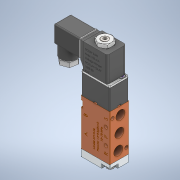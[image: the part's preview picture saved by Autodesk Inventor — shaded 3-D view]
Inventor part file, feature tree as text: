
AUTODESK INVENTOR PART (.ipt)
format: ipt  version: 2020 (Build 240168000, 168)  size: 15,170,048 bytes
history: native  units: in
note: dims shown in document units (in); Inventor stores cm internally (conversion verified against a paired STEP export)
features: other x76, pattern_circular x1, sketch x1
ambient origin geometry x8: Origin, YZ Plane, XZ Plane, XY Plane, X Axis, Y Axis, Z Axis, Center Point
bodies: Solid1 (feature_tree), Solid2 (feature_tree), Solid3 (feature_tree), Solid4 (feature_tree), Solid5 (feature_tree), Solid6 (feature_tree), Solid7 (feature_tree), Solid8 (feature_tree), Solid9 (feature_tree), Solid10 (feature_tree), Solid11 (feature_tree), Solid12 (feature_tree), Solid13 (feature_tree), Solid14 (feature_tree), Solid15 (feature_tree), Solid16 (feature_tree), Solid17 (feature_tree), Solid18 (feature_tree), Solid19 (feature_tree), Solid20 (feature_tree), Solid21 (feature_tree), Solid22 (feature_tree), Solid23 (feature_tree), Solid24 (feature_tree), Solid25 (feature_tree), Solid26 (feature_tree), Solid27 (feature_tree), Solid28 (feature_tree), Solid29 (feature_tree), Solid30 (feature_tree), Solid31 (feature_tree), Solid32 (feature_tree), Solid33 (feature_tree), Solid34 (feature_tree), Solid35 (feature_tree), Solid36 (feature_tree), Solid37 (feature_tree), Solid38 (feature_tree), Solid39 (feature_tree), Solid40 (feature_tree), Solid41 (feature_tree), Solid42 (feature_tree), Solid43 (feature_tree), Solid44 (feature_tree), Solid45 (feature_tree), Solid46 (feature_tree), Solid47 (feature_tree), Solid48 (feature_tree), Solid49 (feature_tree), Solid50 (feature_tree), Solid51 (feature_tree), Solid52 (feature_tree), Solid53 (feature_tree), Solid54 (feature_tree), Solid55 (feature_tree), Solid56 (feature_tree), Solid57 (feature_tree), Solid58 (feature_tree), Solid59 (feature_tree), Solid60 (feature_tree), Solid61 (feature_tree), Solid62 (feature_tree), Solid63 (feature_tree), Solid64 (feature_tree), Solid65 (feature_tree), Solid66 (feature_tree), Solid67 (feature_tree), Solid68 (feature_tree), Solid69 (feature_tree), Solid70 (feature_tree), Solid71 (feature_tree), Solid72 (feature_tree), Solid73 (feature_tree), Solid74 (feature_tree), Solid75 (feature_tree), Solid76 (feature_tree), Solid77 (feature_tree), Solid78 (feature_tree), Solid79 (feature_tree), Solid80 (feature_tree), Solid81 (feature_tree), Solid82 (feature_tree), Solid83 (feature_tree), Solid84 (feature_tree), Solid85 (feature_tree), Solid86 (feature_tree)
feature tree (78):
  other  "Repaired Geometry1"
  pattern_circular  "Circular Pattern1"  Count=2 Angle=360.0deg
  sketch  "3D Sketch14"
  other  "Pattern of Solid36:1"
  other  "Pattern of Solid37:2"
  other  "Pattern of Solid38:3"
  other  "Pattern of Solid39:4"
  other  "Pattern of Solid40:5"
  other  "Pattern of Solid41:6"
  other  "Pattern of Solid42:7"
  other  "Pattern of Solid43:8"
  other  "Pattern of Solid44:9"
  other  "Pattern of Solid45:10"
  other  "Pattern of Solid46:11"
  other  "Pattern of Solid47:12"
  other  "Pattern of Solid48:13"
  other  "Pattern of Solid49:14"
  other  "Pattern of Solid50:15"
  other  "Pattern of Solid51:16"
  other  "Pattern of Solid52:17"
  other  "Pattern of Solid53:18"
  other  "Pattern of Solid54:19"
  other  "Pattern of Solid55:20"
  other  "VALVE BODY, 4V110-06, 2 POSITION, 5 WAY SOLENOID VALVE_74:1"
  other  "ACTUATING SHAFT, 4V110-06, 2 POSITION, 5 WAY SOLENOID VALVE_75:1"
  other  "O-RING, ACTUATING SHAFT, 4V110-06, 2 POSITION, 5 WAY SOLENOID VALVE_76:1"
  other  "O-RING, ACTUATING SHAFT, 4V110-06, 2 POSITION, 5 WAY SOLENOID VALVE_77:1"
  other  "LARGE O-RING, ACTUATING SHAFT, 4V110-06, 2 POSITION, 5 WAY SOLENOID VALVE_78:1"
  other  "INTERNAL SPRING, VALVE BODY SUBASSY, 4V110-06, 2 POSITION, 5 WAY SOLENOID VALVE_79:1"
  other  "SEALING BASE, VALVE BODY SUBASSY, 4V110-06, 2 POSITION, 5 WAY SOLENOID VALVE_80:1"
  other  "O-RING, SEALING BASE, VALVE BODY SUBASSY, 4V110-06, 2 POSITION, 5 WAY SOLENOID VALVE_81:1"
  other  "LARGE O-RING, ACTUATING SHAFT, 4V110-06, 2 POSITION, 5 WAY SOLENOID VALVE_86:1"
  other  "O-RING, ACTUATING SHAFT, 4V110-06, 2 POSITION, 5 WAY SOLENOID VALVE_87:1"
  other  "O-RING, ACTUATING SHAFT, 4V110-06, 2 POSITION, 5 WAY SOLENOID VALVE_88:1"
  other  "AIR ENTRY MANIFOLD, AIR DELIVERY SUBASSY, 4V110-06, 2 POSITION, 5 WAY SOLENOID VALVE_62:1"
  other  "SEAL PLATE, AIR DELIVERY SUBASSY, 4V110-06, 2 POSITION, 5 WAY SOLENOID VALVE_63:1"
  other  "SEAL, AIR DELIVERY SUBASSY, 4V110-06, 2 POSITION, 5 WAY SOLENOID VALVE_64:1"
  other  "LEVER, MANUAL CONTROL SUBASSY, 4V110-06, 2 POSITION, 5 WAY SOLENOID VALVE_71:1"
  other  "O-RING, MANUAL CONTROL SUBASSY, 4V110-06, 2 POSITION, 5 WAY SOLENOID VALVE_72:1"
  other  "SPRING, MANUAL CONTROL SUBASSY, 4V110-06, 2 POSITION, 5 WAY SOLENOID VALVE_73:1"
  other  "AIR LOCK TAB, AIR DELIVERY SUBASSY, 4V110-06, 2 POSITION, 5 WAY SOLENOID VALVE_66:1"
  other  "O-RING, AIR DELIVERY SUBASSY, 4V110-06, 2 POSITION, 5 WAY SOLENOID VALVE_67:1"
  other  "COMPRESSING PLATE, 4V110-06, 2 POSITION, 5 WAY SOLENOID VALVE_68:1"
  other  "MANIFOLD SEALING PIN, AIR DELIVERY SUBASSY, 4V110-06, 2 POSITION, 5 WAY SOLENOID VALVE_69:1"
  other  "MANIFOLD SEALING PIN, AIR DELIVERY SUBASSY, 4V110-06, 2 POSITION, 5 WAY SOLENOID VALVE_70:1"
  other  "SOLENOID CASE, ELECTRICAL SUBASSY, 4V110-06, 2 POSITION, 5 WAY SOLENOID VALVE_53:1"
  other  "SOLENOID CASE COVER, ELECTRICAL SUBASSY, 4V110-06, 2 POSITION, 5 WAY SOLENOID VALVE_54:1"
  other  "SOLENOID BOBBIN, ELECTRICAL SUBASSY, 4V110-06, 2 POSITION, 5 WAY SOLENOID VALVE_55:1"
  other  "COVER, SOLENOID SUBASSY, ELECTRICAL SUBASSY, 4V110-06, 2 POSITION, 5 WAY SOLENOID VALVE_56:1"
  other  "GROUND CONNECTOR, ELECTRICAL SUBASSY, 4V110-06, 2 POSITION, 5 WAY SOLENOID VALVE_57:1"
  other  "ELECTRICAL CONNECTOR, ELECTRICAL SUBASSY, 4V110-06, 2 POSITION, 5 WAY SOLENOID VALVE_58:1"
  other  "ELECTRICAL CONNECTOR, ELECTRICAL SUBASSY, 4V110-06, 2 POSITION, 5 WAY SOLENOID VALVE_59:1"
  other  "M3 THREADED INSERT, ELECTRICAL SUBASSY, 4V110-06, 2 POSITION, 5 WAY SOLENOID VALVE_60:1"
  other  "SOLENOID BOBBIN BOTTOM HALF, ELECTRICAL SUBASSY, 4V110-06, 2 POSITION, 5 WAY SOLENOID VALVE_61:1"
  other  "ELECTRICAL ENCLOSURE, ELECTRICAL SUBASSY, 4V110-06, 2 POSITION, 5 WAY SOLENOID VALVE_40:1"
  other  "FLAT GASKET, ELECTRICAL SUBASSY, 4V110-06, 2 POSITION, 5 WAY SOLENOID VALVE_41:1"
  other  "WASHER GASKET, ELECTRICAL SUBASSY, 4V110-06, 2 POSITION, 5 WAY SOLENOID VALVE_42:1"
  other  "WIRING NUT, ELECTRICAL SUBASSY, 4V110-06, 2 POSITION, 5 WAY SOLENOID VALVE_43:1"
  other  "RECEPTACLE, ELECTRICAL SUBASSY, 4V110-06, 2 POSITION, 5 WAY SOLENOID VALVE_44:1"
  other  "PCB, ELECTRICAL SUBASSY, 4V110-06, 2 POSITION, 5 WAY SOLENOID VALVE_46:1"
  other  "PCB, ELECTRICAL SUBASSY, 4V110-06, 2 POSITION, 5 WAY SOLENOID VALVE_46:2"
  other  "PCB, ELECTRICAL SUBASSY, 4V110-06, 2 POSITION, 5 WAY SOLENOID VALVE_46:3"
  other  "PCB, ELECTRICAL SUBASSY, 4V110-06, 2 POSITION, 5 WAY SOLENOID VALVE_46:4"
  other  "PCB, ELECTRICAL SUBASSY, 4V110-06, 2 POSITION, 5 WAY SOLENOID VALVE_46:5"
  other  "TERMINAL CONNECTOR, ELECTRICAL SUBASSY, 4V110-06, 2 POSITION, 5 WAY SOLENOID VALVE_50:1"
  other  "TERMINAL CONNECTOR, ELECTRICAL SUBASSY, 4V110-06, 2 POSITION, 5 WAY SOLENOID VALVE_50:2"
  other  "TERMINAL CONNECTOR, ELECTRICAL SUBASSY, 4V110-06, 2 POSITION, 5 WAY SOLENOID VALVE_50:3"
  other  "ARMATURE HOLDING BODY, 4V110-06, 2 POSITION, 5 WAY SOLENOID VALVE_36:1"
  other  "ARMATURE PULLING CORE, 4V110-06, 2 POSITION, 5 WAY SOLENOID VALVE_37:1"
  other  "O-RING, 4V110-06, 2 POSITION, 5 WAY SOLENOID VALVE_38:1"
  other  "ARMATURE BODY, 4V110-06, 2 POSITION, 5 WAY SOLENOID VALVE_31:1"
  other  "TOP CAP, ARMATURE BODY, 4V110-06, 2 POSITION, 5 WAY SOLENOID VALVE_32:1"
  other  "BOTTOM CAP, ARMATURE BODY, 4V110-06, 2 POSITION, 5 WAY SOLENOID VALVE_33:1"
  other  "SPRING, ARMATURE SUBASSY, 4V110-06, 2 POSITION, 5 WAY SOLENOID VALVE_34:1"
  other  "INTERNAL SPRING, ARMATURE SUBASSY, 4V110-06, 2 POSITION, 5 WAY SOLENOID VALVE_35:1"
  other  "M3X25, FLAT HEAD PHILLIPS MACHINE SCREW, 4V110-06, 2 POSITION, 5 WAY SOLENOID VALVE_default_28:1"
  other  "M3X25, FLAT HEAD PHILLIPS MACHINE SCREW, 4V110-06, 2 POSITION, 5 WAY SOLENOID VALVE_default_29:1"
  other  "M6 HEX NUT WITH EXTENDED BODY, 4V110-06, 2 POSITION, 5 WAY SOLENOID VALVE_default_30:1"
